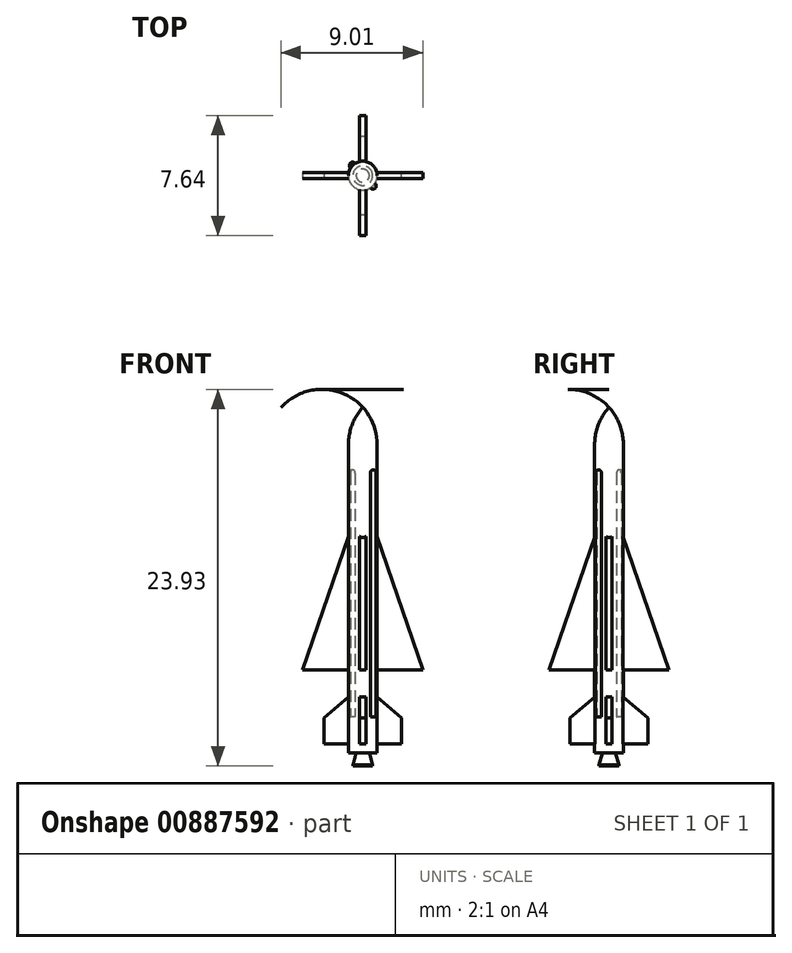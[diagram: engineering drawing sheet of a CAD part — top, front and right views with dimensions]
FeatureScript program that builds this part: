
annotation { "Feature Type Name" : "Feature", "Feature Type Description" : "" }
export const myFeature = defineFeature(function(context is Context, id is Id, definition is map)
    precondition{}
    {
        {
            assignVariable(context, id + "F0", {"name" : "s", "anyValue" : 144});
        }
        {
            var Q0;
            Q0=qCreatedBy(makeId("Front.planeOp"),FACE);
            var sketch = newSketch(context, id + "F1", { "sketchPlane" : qUnion([Q0])});
            skLineSegment(sketch, "E0", {"start": v(0, 0) * mm, "end": v(0, 22.78) * mm});
            skLineSegment(sketch, "E1", {"start": v(0.91, 20.42) * mm, "end": v(0.91, 0) * mm});
            skLineSegment(sketch, "E2", {"start": v(0.91, 0) * mm, "end": v(0, 0) * mm});
            skArc(sketch, "E3", {"start": v(0.91, 20.42) * mm, "mid": v(0.68, 21.68) * mm, "end": v(0, 22.78) * mm});
            skLineSegment(sketch, "E4", {"start": v(0.62, 0) * mm, "end": v(0.62, 0.07) * mm});
            skLineSegment(sketch, "E5", {"start": v(0.62, 0.07) * mm, "end": v(0.42, 0.83) * mm});
            skLineSegment(sketch, "E6", {"start": v(0.42, 0.83) * mm, "end": v(0.91, 0.83) * mm});
            skSolve(sketch);
        }
        {
            var Q0;
            {var subQ0=sQuery(id+"F1.wireOp",EDGE,"mrwio9nY-PsAZ-Zbfy-NhIU-sYq0QVbgGXAG");Q0=makeQuery(id+"F1.imprint","IMPRINT",FACE,{"disambiguationData":[TD([[makeQuery(id+"F1.imprint","IMPRINT",EDGE,{"derivedFrom":subQ0}),-1.0]])]});}
            var Q1;
            Q1=makeQuery(id+"F1.imprint","IMPRINT",FACE,{"disambiguationData":[TD([[makeQuery(id+"F1.imprint","IMPRINT",EDGE,{"derivedFrom":sQuery(id+"F1.wireOp",EDGE,"rEedh4zr-IGRr-Hqzj-sDLB-QnI7VE1V64O6.bottom")}),-1.0]])]});
            var Q2;
            Q2=makeQuery(id+"F1.imprint","IMPRINT",FACE,{"disambiguationData":[TD([[makeQuery(id+"F1.imprint","IMPRINT",EDGE,{"derivedFrom":sQuery(id+"F1.wireOp",EDGE,"E0")}),-1.0]])]});
            var Q3;
            Q3=makeQuery(id+"F1.imprint","IMPRINT",FACE,{"disambiguationData":[TD([[makeQuery(id+"F1.imprint","IMPRINT",EDGE,{"derivedFrom":sQuery(id+"F1.wireOp",EDGE,"p5wuz8j9-3HT4-kWwn-DjtP-lJmqTNSXSBJY.bottom")}),-1.0]])]});
            var Q4;
            Q4=sQuery(id+"F1.wireOp",EDGE,"E0");
            revolve(context, id + "F2", {"surfaceOperationType" : NewSurfaceOperationType.NEW, "entities" : qUnion([Q0, Q1, Q2, Q3]), "axis" : qUnion([Q4]), "revolveType" : RevolveType.FULL});
        }
        {
            var Q0;
            Q0=qCreatedBy(makeId("Front.planeOp"),FACE);
            var sketch = newSketch(context, id + "F3", { "sketchPlane" : qUnion([Q0])});
            skLineSegment(sketch, "E7", {"start": v(0, 0) * mm, "end": v(0, 15.4) * mm});
            skLineSegment(sketch, "E8", {"start": v(3.82, 6.11) * mm, "end": v(0.4, 6.11) * mm});
            skLineSegment(sketch, "E9", {"start": v(0.4, 6.11) * mm, "end": v(0.4, 4.81) * mm});
            skLineSegment(sketch, "E10", {"start": v(0.4, 4.81) * mm, "end": v(2.47, 3.06) * mm});
            skLineSegment(sketch, "E11", {"start": v(2.47, 3.06) * mm, "end": v(2.47, 1.39) * mm});
            skLineSegment(sketch, "E12", {"start": v(0.91, 0) * mm, "end": v(0.91, 32.87) * mm, "construction": true});
            skPoint(sketch, "E13", {"position": v(0.91, 4.38) * mm});
            skPoint(sketch, "E14", {"position": v(0.91, 6.11) * mm});
            skLineSegment(sketch, "E15", {"start": v(2.47, 1.39) * mm, "end": v(0, 1.39) * mm});
            skLineSegment(sketch, "E16", {"start": v(3.82, 6.11) * mm, "end": v(0.6, 15.4) * mm});
            skLineSegment(sketch, "E17", {"start": v(0.6, 15.4) * mm, "end": v(0, 15.4) * mm});
            skLineSegment(sketch, "E18.0", {"start": v(0.91, 0.83) * mm, "end": v(-0.91, 0.83) * mm});
            skPoint(sketch, "E19", {"position": v(0.91, 14.51) * mm});
            skSolve(sketch);
        }
        {
            var Q0;
            Q0=qSketchRegion(id+"F3",true);
            extrude(context, id + "F4", {"entities" : qUnion([Q0]), "operationType" : NewBodyOperationType.ADD, "depth" : .4 * mm, "offsetDistance" : 25 * mm, "symmetric" : true});
        }
        {
            var Q0;
            Q0=makeQuery(id+"F2.opRevolve","SWEPT_BODY",BODY,{"disambiguationData":[OSD([sQuery(id+"F1.wireOp",EDGE,"E0"),sQuery(id+"F1.wireOp",EDGE,"E1"),sQuery(id+"F1.wireOp",EDGE,"E2"),sQuery(id+"F1.wireOp",EDGE,"2EiOItwe-9FNA-eY8p-DkXH-AMy5AHyUmzZA"),sQuery(id+"F1.wireOp",EDGE,"E3")])]});
            var Q1;
            Q1=makeQuery(id+"F2.opRevolve","SWEPT_FACE",FACE,{"disambiguationData":[OSD([sQuery(id+"F1.wireOp",EDGE,"E1")])]});
            circularPattern(context, id + "F5", {"operationType" : NewBodyOperationType.ADD, "entities" : qUnion([Q0]), "axis" : qUnion([Q1]), "angle" : 360 * degree, "instanceCount" : 4, "equalSpace" : true, "computeTransformsWithoutBuiltin" : true});
        }
        {
            var Q0;
            Q0=qCreatedBy(makeId("Top.planeOp"),FACE);
            cPlane(context, id + "F6", {"entities" : qUnion([Q0]), "cplaneType" : CPlaneType.OFFSET, "offset" : (450 / getVariable(context, 's')) * mm, "width" : 150 * mm, "height" : 150 * mm});
        }
        {
            var Q0;
            Q0=qCreatedBy(id+"F6.planeOp",FACE);
            var sketch = newSketch(context, id + "F7", { "sketchPlane" : qUnion([Q0])});
            skCircle(sketch, "E20.0", {"center": v(0, 0) * mm, "radius": 0.91 * mm});
            skLineSegment(sketch, "E21", {"start": v(0.25, -0.55) * mm, "end": v(0.5, -0.8) * mm});
            skLineSegment(sketch, "E22", {"start": v(0.8, -0.5) * mm, "end": v(0.55, -0.25) * mm});
            skLineSegment(sketch, "E23", {"start": v(0.55, -0.25) * mm, "end": v(0.25, -0.55) * mm});
            skLineSegment(sketch, "E24", {"start": v(0.78, 0) * mm, "end": v(0, 0) * mm, "construction": true});
            skLineSegment(sketch, "E25", {"start": v(0.4, -0.4) * mm, "end": v(0, 0) * mm, "construction": true});
            skArc(sketch, "E26", {"start": v(0.5, -0.8) * mm, "mid": v(0.8, -0.8) * mm, "end": v(0.8, -0.5) * mm});
            skLineSegment(sketch, "E27", {"start": v(0, 0) * mm, "end": v(-0.36, -0.36) * mm, "construction": true});
            skLineSegment(sketch, "E28.MirrorCS", {"start": v(-0.55, 0.25) * mm, "end": v(-0.8, 0.5) * mm});
            skLineSegment(sketch, "E29.MirrorCS", {"start": v(-0.25, 0.55) * mm, "end": v(-0.55, 0.25) * mm});
            skLineSegment(sketch, "E30.MirrorCS", {"start": v(-0.5, 0.8) * mm, "end": v(-0.25, 0.55) * mm});
            skArc(sketch, "E31.MirrorCS", {"start": v(-0.8, 0.5) * mm, "mid": v(-0.8, 0.8) * mm, "end": v(-0.5, 0.8) * mm});
            skSolve(sketch);
        }
        {
            var Q0;
            Q0 = qSketchRegion(id + "F7", true);
            extrude(context, id + "F8", {"entities" : qUnion([Q0]), "operationType" : NewBodyOperationType.ADD, "depth" : (2260 / getVariable(context, 's')) * mm, "offsetDistance" : 25 * mm});
        }
        {
            var Q0;
            Q0=makeQuery(id+"F8.opExtrude","CAP_EDGE",EDGE,{"disambiguationData":[OSD([sQuery(id+"F7.wireOp",EDGE,"E31.MirrorCS")])],"isStart":false});
            var Q1;
            Q1=makeQuery(id+"F8.opExtrude","CAP_EDGE",EDGE,{"disambiguationData":[OSD([sQuery(id+"F7.wireOp",EDGE,"E26")])],"isStart":false});
            fillet(context, id + "F9", {"entities" : qUnion([Q0, Q1]), "radius" : (30 / getVariable(context, 's')) * mm, "tangentPropagation" : true, "allowEdgeOverflow" : false});
        }
    });
